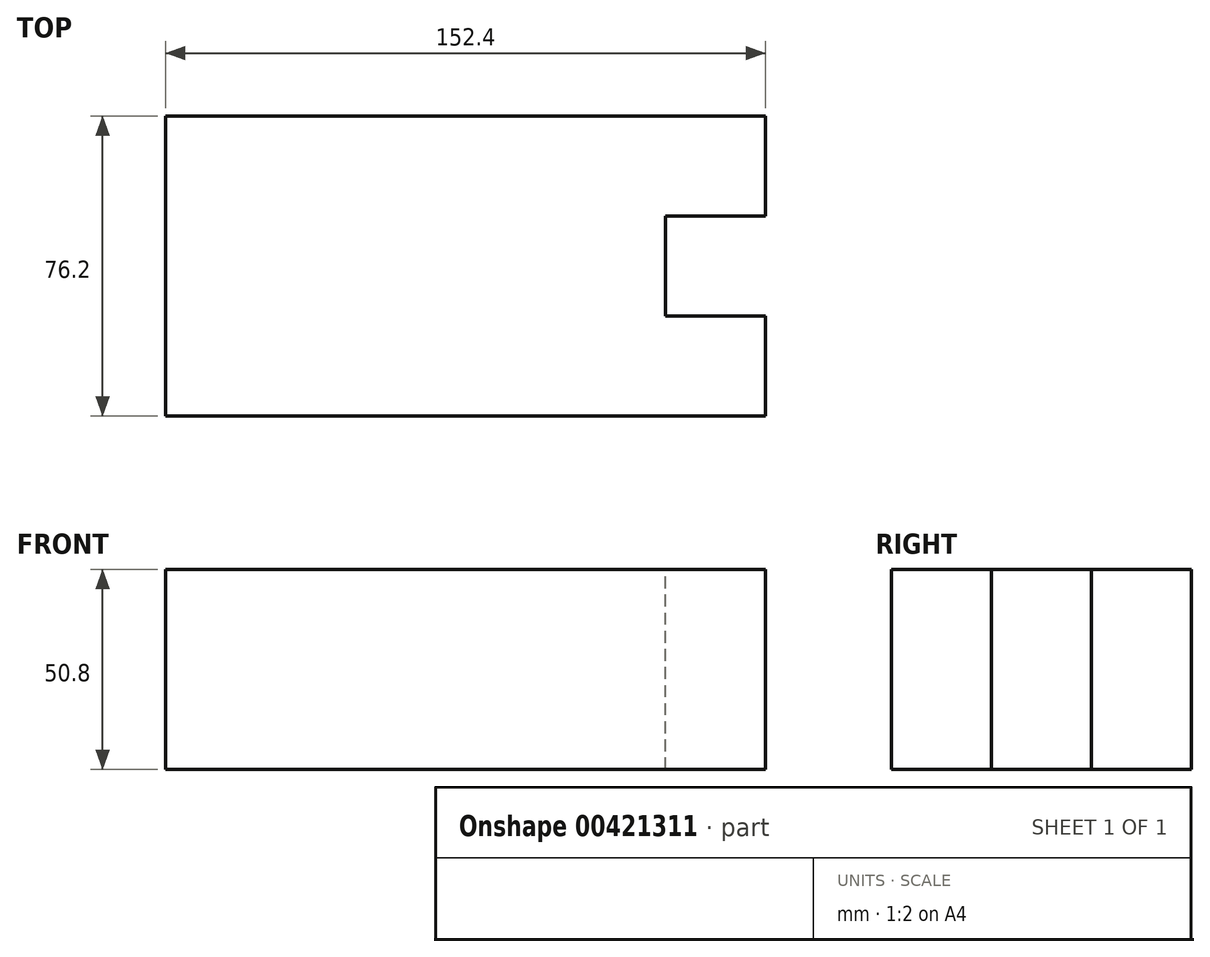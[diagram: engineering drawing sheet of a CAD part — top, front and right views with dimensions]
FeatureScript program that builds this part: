
annotation { "Feature Type Name" : "Feature", "Feature Type Description" : "" }
export const myFeature = defineFeature(function(context is Context, id is Id, definition is map)
    precondition{}
    {
        {
            var Q0;
            Q0=qCreatedBy(makeId("Top.planeOp"),FACE);
            var sketch = newSketch(context, id + "F0", { "sketchPlane" : qUnion([Q0])});
            skLineSegment(sketch, "E0", {"start": v(0, 0) * mm, "end": v(152.4, 0) * mm});
            skLineSegment(sketch, "E1", {"start": v(0, 0) * mm, "end": v(0, 76.2) * mm});
            skLineSegment(sketch, "E2", {"start": v(0, 76.2) * mm, "end": v(152.4, 76.2) * mm});
            skLineSegment(sketch, "E3", {"start": v(152.4, 76.2) * mm, "end": v(152.4, 50.8) * mm});
            skLineSegment(sketch, "E4", {"start": v(152.4, 0) * mm, "end": v(152.4, 25.4) * mm});
            skLineSegment(sketch, "E5", {"start": v(152.4, 50.8) * mm, "end": v(127, 50.8) * mm});
            skLineSegment(sketch, "E6", {"start": v(152.4, 25.4) * mm, "end": v(127, 25.4) * mm});
            skLineSegment(sketch, "E7", {"start": v(127, 50.8) * mm, "end": v(127, 25.4) * mm});
            skSolve(sketch);
        }
        {
            var Q0;
            Q0=makeQuery(id+"F0.imprint","IMPRINT",FACE,{"disambiguationData":[TD([[makeQuery(id+"F0.imprint","IMPRINT",EDGE,{"derivedFrom":sQuery(id+"F0.wireOp",EDGE,"E0")}),1.0]])]});
            extrude(context, id + "F1", {"entities" : qUnion([Q0]), "oppositeDirection" : true, "depth" : 50.8 * mm});
        }
    });
